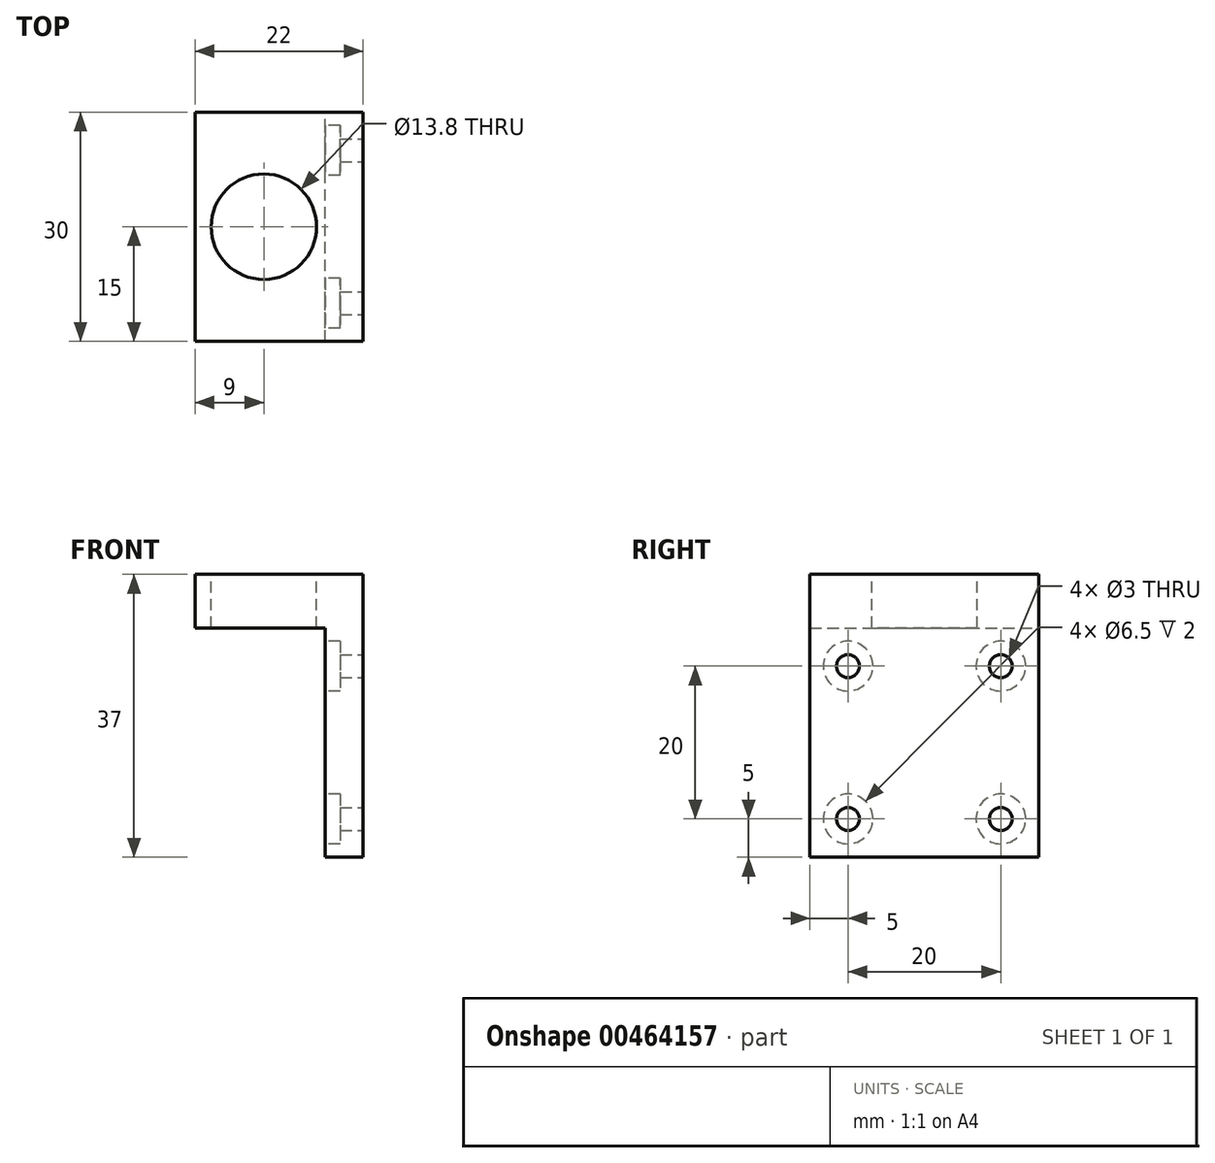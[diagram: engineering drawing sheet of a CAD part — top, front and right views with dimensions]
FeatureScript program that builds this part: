
annotation { "Feature Type Name" : "Feature", "Feature Type Description" : "" }
export const myFeature = defineFeature(function(context is Context, id is Id, definition is map)
    precondition{}
    {
        {
            var Q0;
            Q0=qCreatedBy(makeId("Top.planeOp"),FACE);
            var sketch = newSketch(context, id + "F0", { "sketchPlane" : qUnion([Q0])});
            skLineSegment(sketch, "E0.bottom", {"start": v(0, 0) * mm, "end": v(22, 0) * mm});
            skLineSegment(sketch, "E0.top", {"start": v(0, 30) * mm, "end": v(22, 30) * mm});
            skLineSegment(sketch, "E0.left", {"start": v(0, 0) * mm, "end": v(0, 30) * mm});
            skLineSegment(sketch, "E0.right", {"start": v(22, 0) * mm, "end": v(22, 30) * mm});
            skSolve(sketch);
        }
        {
            var Q0;
            Q0 = qSketchRegion(id + "F0", true);
            extrude(context, id + "F1", {"entities" : qUnion([Q0]), "depth" : 7 * mm});
        }
        {
            var Q0;
            Q0=makeQuery(id+"F1.opExtrude","CAP_FACE",FACE,{"disambiguationData":[OSD([sQuery(id+"F0.wireOp",EDGE,"E0.bottom"),sQuery(id+"F0.wireOp",EDGE,"E0.top"),sQuery(id+"F0.wireOp",EDGE,"E0.left"),sQuery(id+"F0.wireOp",EDGE,"E0.right")])],"isStart":false});
            var sketch = newSketch(context, id + "F2", { "sketchPlane" : qUnion([Q0])});
            skCircle(sketch, "E1", {"center": v(9, 15) * mm, "radius": 6.9 * mm});
            skSolve(sketch);
        }
        {
            var Q0;
            Q0 = qSketchRegion(id + "F2", true);
            extrude(context, id + "F3", {"entities" : qUnion([Q0]), "operationType" : NewBodyOperationType.REMOVE, "oppositeDirection" : true, "depth" : 25 * mm});
        }
        {
            var Q0;
            Q0=makeQuery(id+"F1.opExtrude","CAP_FACE",FACE,{"disambiguationData":[OSD([sQuery(id+"F0.wireOp",EDGE,"E0.bottom"),sQuery(id+"F0.wireOp",EDGE,"E0.top"),sQuery(id+"F0.wireOp",EDGE,"E0.left"),sQuery(id+"F0.wireOp",EDGE,"E0.right")])],"isStart":true});
            var sketch = newSketch(context, id + "F4", { "sketchPlane" : qUnion([Q0])});
            skLineSegment(sketch, "E2.bottom", {"start": v(22, 0) * mm, "end": v(17, 0) * mm});
            skLineSegment(sketch, "E2.top", {"start": v(22, -30) * mm, "end": v(17, -30) * mm});
            skLineSegment(sketch, "E2.left", {"start": v(22, 0) * mm, "end": v(22, -30) * mm});
            skLineSegment(sketch, "E2.right", {"start": v(17, 0) * mm, "end": v(17, -30) * mm});
            skSolve(sketch);
        }
        {
            var Q0;
            Q0 = qSketchRegion(id + "F4", true);
            extrude(context, id + "F5", {"entities" : qUnion([Q0]), "operationType" : NewBodyOperationType.ADD, "depth" : 30 * mm});
        }
        {
            var Q0;
            Q0=makeQuery(id+"F5.boolean.opBoolean","MERGE",FACE,{"derivedFrom":[makeQuery(id+"F1.opExtrude","SWEPT_FACE",FACE,{"disambiguationData":[OSD([sQuery(id+"F0.wireOp",EDGE,"E0.right")])]}),makeQuery(id+"F5.opExtrude","SWEPT_FACE",FACE,{"disambiguationData":[OSD([sQuery(id+"F4.wireOp",EDGE,"E2.left")])]})]});
            var sketch = newSketch(context, id + "F6", { "sketchPlane" : qUnion([Q0])});
            skCircle(sketch, "E3", {"center": v(5, -25) * mm, "radius": 1.5 * mm});
            skCircle(sketch, "E4", {"center": v(25, -25) * mm, "radius": 1.5 * mm});
            skCircle(sketch, "E5", {"center": v(25, -5) * mm, "radius": 1.5 * mm});
            skCircle(sketch, "E6", {"center": v(5, -5) * mm, "radius": 1.5 * mm});
            skSolve(sketch);
        }
        {
            var Q0;
            Q0 = qSketchRegion(id + "F6", true);
            extrude(context, id + "F7", {"entities" : qUnion([Q0]), "operationType" : NewBodyOperationType.REMOVE, "oppositeDirection" : true, "depth" : 25 * mm});
        }
        {
            var Q0;
            Q0=makeQuery(id+"F5.opExtrude","SWEPT_FACE",FACE,{"disambiguationData":[OSD([sQuery(id+"F4.wireOp",EDGE,"E2.right")])]});
            var sketch = newSketch(context, id + "F8", { "sketchPlane" : qUnion([Q0])});
            skCircle(sketch, "E7", {"center": v(-25, -5) * mm, "radius": 3.25 * mm});
            skCircle(sketch, "E8", {"center": v(-5, -5) * mm, "radius": 3.25 * mm});
            skCircle(sketch, "E9", {"center": v(-5, -25) * mm, "radius": 3.25 * mm});
            skCircle(sketch, "E10", {"center": v(-25, -25) * mm, "radius": 3.25 * mm});
            skSolve(sketch);
        }
        {
            var Q0;
            Q0 = qSketchRegion(id + "F8", true);
            extrude(context, id + "F9", {"entities" : qUnion([Q0]), "operationType" : NewBodyOperationType.REMOVE, "oppositeDirection" : true, "depth" : 2 * mm});
        }
    });
